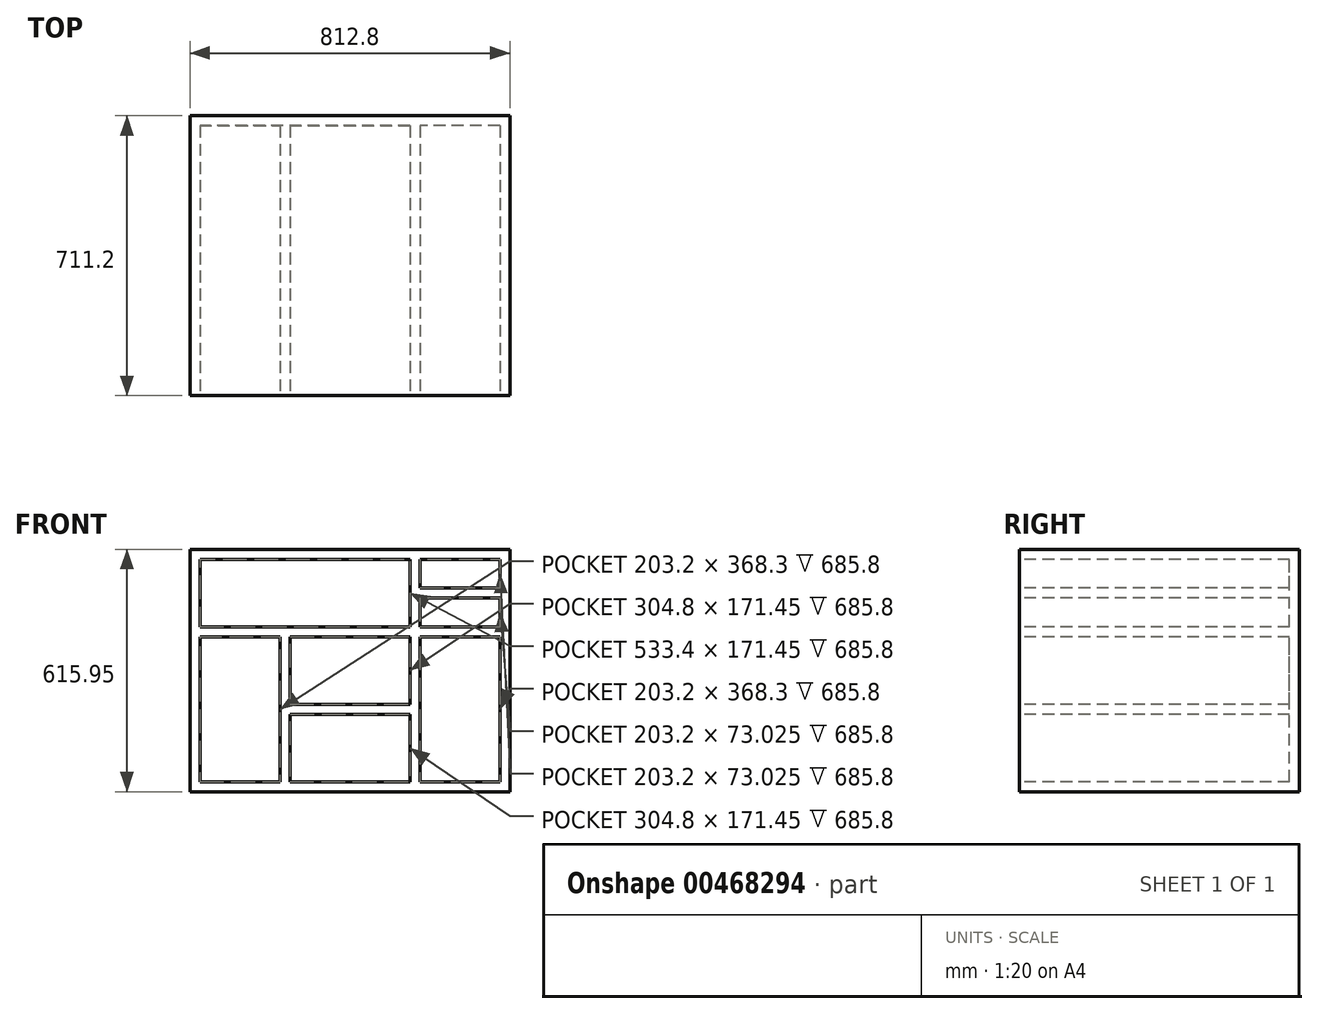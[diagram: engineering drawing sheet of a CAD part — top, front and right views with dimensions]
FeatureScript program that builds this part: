
annotation { "Feature Type Name" : "Feature", "Feature Type Description" : "" }
export const myFeature = defineFeature(function(context is Context, id is Id, definition is map)
    precondition{}
    {
        {
            var Q0;
            Q0=qCreatedBy(makeId("Front.planeOp"),FACE);
            var sketch = newSketch(context, id + "F0", { "sketchPlane" : qUnion([Q0])});
            skLineSegment(sketch, "E0.bottom", {"start": v(0, 0) * mm, "end": v(812.8, 0) * mm});
            skLineSegment(sketch, "E0.top", {"start": v(0, 615.95) * mm, "end": v(812.8, 615.95) * mm});
            skLineSegment(sketch, "E0.left", {"start": v(0, 0) * mm, "end": v(0, 615.95) * mm});
            skLineSegment(sketch, "E0.right", {"start": v(812.8, 0) * mm, "end": v(812.8, 615.95) * mm});
            skSolve(sketch);
        }
        {
            var Q0;
            Q0=qSketchRegion(id+"F0",true);
            extrude(context, id + "F1", {"entities" : qUnion([Q0]), "depth" : 711.2 * mm});
        }
        {
            var Q0;
            Q0=makeQuery(id+"F1.opExtrude","CAP_FACE",FACE,{"disambiguationData":[OSD([sQuery(id+"F0.wireOp",EDGE,"E0.bottom"),sQuery(id+"F0.wireOp",EDGE,"E0.top"),sQuery(id+"F0.wireOp",EDGE,"E0.left"),sQuery(id+"F0.wireOp",EDGE,"E0.right")])],"isStart":false});
            var sketch = newSketch(context, id + "F2", { "sketchPlane" : qUnion([Q0])});
            skLineSegment(sketch, "E1.bottom", {"start": v(25.4, 25.4) * mm, "end": v(228.6, 25.4) * mm});
            skLineSegment(sketch, "E1.top", {"start": v(25.4, 393.7) * mm, "end": v(228.6, 393.7) * mm});
            skLineSegment(sketch, "E1.left", {"start": v(25.4, 25.4) * mm, "end": v(25.4, 393.7) * mm});
            skLineSegment(sketch, "E1.right", {"start": v(228.6, 25.4) * mm, "end": v(228.6, 393.7) * mm});
            skLineSegment(sketch, "E2.bottom", {"start": v(787.4, 25.4) * mm, "end": v(584.2, 25.4) * mm});
            skLineSegment(sketch, "E2.top", {"start": v(787.4, 393.7) * mm, "end": v(584.2, 393.7) * mm});
            skLineSegment(sketch, "E2.left", {"start": v(787.4, 25.4) * mm, "end": v(787.4, 393.7) * mm});
            skLineSegment(sketch, "E2.right", {"start": v(584.2, 25.4) * mm, "end": v(584.2, 393.7) * mm});
            skLineSegment(sketch, "E3.bottom", {"start": v(787.4, 419.1) * mm, "end": v(584.2, 419.1) * mm});
            skLineSegment(sketch, "E3.top", {"start": v(787.4, 492.13) * mm, "end": v(584.2, 492.13) * mm});
            skLineSegment(sketch, "E3.left", {"start": v(787.4, 419.1) * mm, "end": v(787.4, 492.13) * mm});
            skLineSegment(sketch, "E3.right", {"start": v(584.2, 419.1) * mm, "end": v(584.2, 492.13) * mm});
            skLineSegment(sketch, "E4.bottom", {"start": v(787.4, 517.53) * mm, "end": v(584.2, 517.53) * mm});
            skLineSegment(sketch, "E4.top", {"start": v(787.4, 590.55) * mm, "end": v(584.2, 590.55) * mm});
            skLineSegment(sketch, "E4.left", {"start": v(787.4, 517.53) * mm, "end": v(787.4, 590.55) * mm});
            skLineSegment(sketch, "E4.right", {"start": v(584.2, 517.53) * mm, "end": v(584.2, 590.55) * mm});
            skLineSegment(sketch, "E5.bottom", {"start": v(558.8, 196.85) * mm, "end": v(254, 196.85) * mm});
            skLineSegment(sketch, "E5.top", {"start": v(558.8, 25.4) * mm, "end": v(254, 25.4) * mm});
            skLineSegment(sketch, "E5.left", {"start": v(558.8, 25.4) * mm, "end": v(558.8, 196.85) * mm});
            skLineSegment(sketch, "E5.right", {"start": v(254, 25.4) * mm, "end": v(254, 196.85) * mm});
            skLineSegment(sketch, "E6.bottom", {"start": v(558.8, 419.1) * mm, "end": v(25.4, 419.1) * mm});
            skLineSegment(sketch, "E6.top", {"start": v(558.8, 590.55) * mm, "end": v(25.4, 590.55) * mm});
            skLineSegment(sketch, "E6.left", {"start": v(558.8, 419.1) * mm, "end": v(558.8, 590.55) * mm});
            skLineSegment(sketch, "E6.right", {"start": v(25.4, 419.1) * mm, "end": v(25.4, 590.55) * mm});
            skLineSegment(sketch, "E7.bottom", {"start": v(254, 222.25) * mm, "end": v(558.8, 222.25) * mm});
            skLineSegment(sketch, "E7.top", {"start": v(254, 393.7) * mm, "end": v(558.8, 393.7) * mm});
            skLineSegment(sketch, "E7.left", {"start": v(254, 222.25) * mm, "end": v(254, 393.7) * mm});
            skLineSegment(sketch, "E7.right", {"start": v(558.8, 222.25) * mm, "end": v(558.8, 393.7) * mm});
            skSolve(sketch);
        }
        {
            var Q0;
            Q0=qSketchRegion(id+"F2",true);
            extrude(context, id + "F3", {"entities" : qUnion([Q0]), "operationType" : NewBodyOperationType.REMOVE, "oppositeDirection" : true, "depth" : 685.8 * mm});
        }
    });
